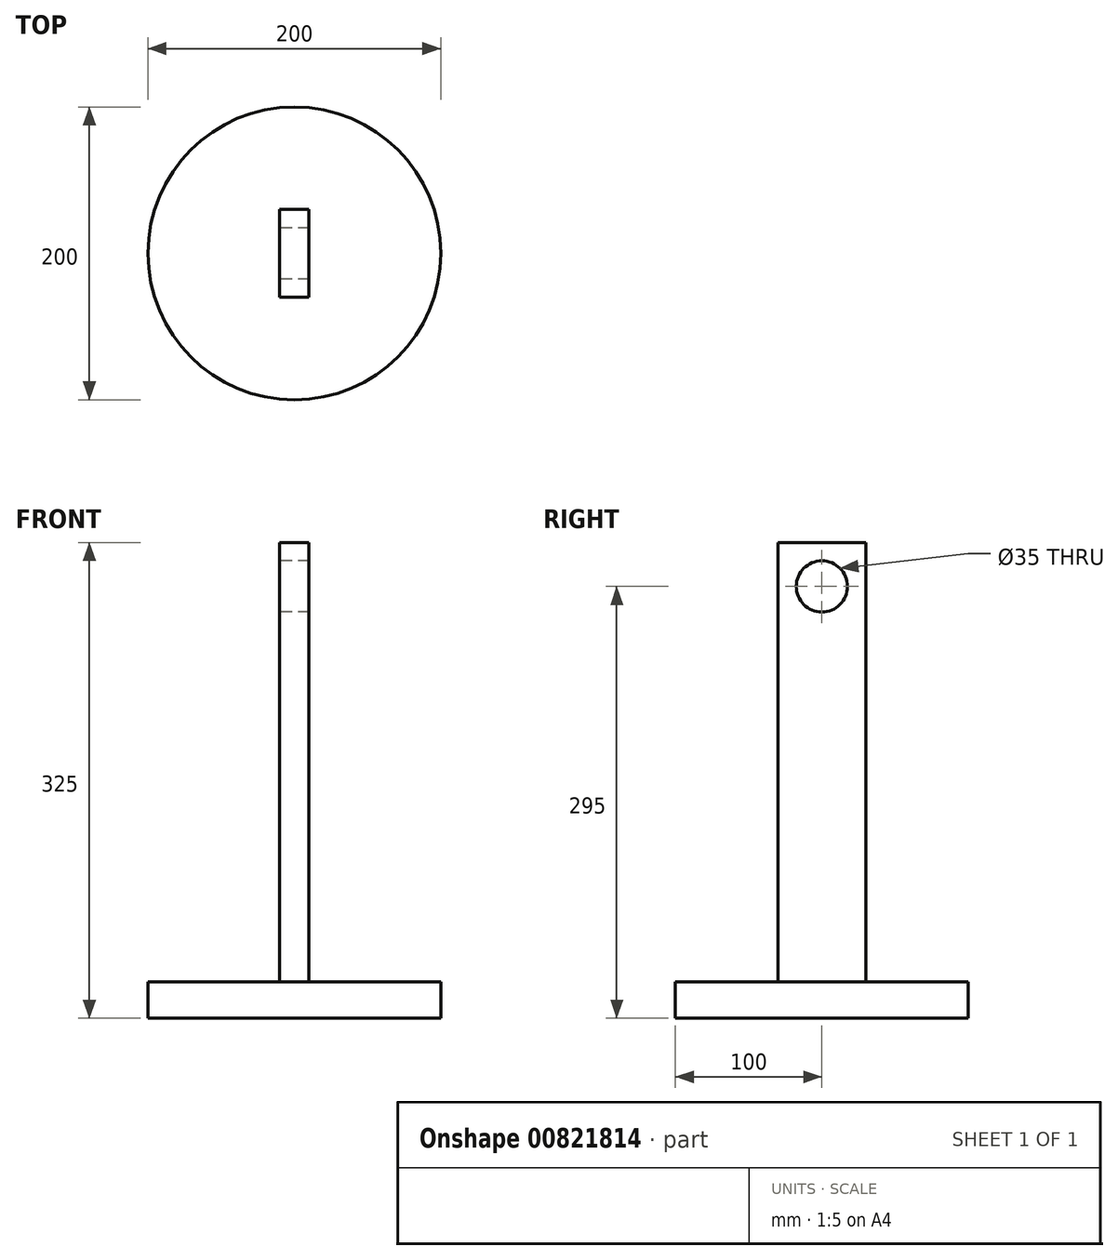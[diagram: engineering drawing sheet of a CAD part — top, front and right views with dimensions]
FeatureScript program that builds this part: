
annotation { "Feature Type Name" : "Feature", "Feature Type Description" : "" }
export const myFeature = defineFeature(function(context is Context, id is Id, definition is map)
    precondition{}
    {
        {
            var Q0;
            Q0=qCreatedBy(makeId("Top.planeOp"),FACE);
            var sketch = newSketch(context, id + "F0", { "sketchPlane" : qUnion([Q0])});
            skCircle(sketch, "E0", {"center": v(0, 0) * mm, "radius": 100 * mm});
            skSolve(sketch);
        }
        {
            var Q0;
            Q0=makeQuery(id+"F0.imprint","IMPRINT",FACE,{"disambiguationData":[TD([[makeQuery(id+"F0.imprint","IMPRINT",EDGE,{"derivedFrom":sQuery(id+"F0.wireOp",EDGE,"E0")}),1.0]])]});
            extrude(context, id + "F1", {"entities" : qUnion([Q0]), "depth" : 25 * mm, "offsetDistance" : 25 * mm});
        }
        {
            var Q0;
            Q0=makeQuery(id+"F1.opExtrude","CAP_FACE",FACE,{"disambiguationData":[OSD([sQuery(id+"F0.wireOp",EDGE,"E0")])],"isStart":false});
            var sketch = newSketch(context, id + "F2", { "sketchPlane" : qUnion([Q0])});
            skLineSegment(sketch, "E1.bottom", {"start": v(10, -30) * mm, "end": v(-10, -30) * mm});
            skLineSegment(sketch, "E1.top", {"start": v(10, 30) * mm, "end": v(-10, 30) * mm});
            skLineSegment(sketch, "E1.left", {"start": v(10, -30) * mm, "end": v(10, 30) * mm});
            skLineSegment(sketch, "E1.right", {"start": v(-10, -30) * mm, "end": v(-10, 30) * mm});
            skPoint(sketch, "E1.middle", {"position": v(0, 0) * mm});
            skSolve(sketch);
        }
        {
            var Q0;
            Q0=makeQuery(id+"F2.imprint","IMPRINT",FACE,{"disambiguationData":[TD([[makeQuery(id+"F2.imprint","IMPRINT",EDGE,{"derivedFrom":sQuery(id+"F2.wireOp",EDGE,"E1.bottom")}),-1.0]])]});
            extrude(context, id + "F3", {"entities" : qUnion([Q0]), "operationType" : NewBodyOperationType.ADD, "depth" : 300 * mm, "offsetDistance" : 25 * mm});
        }
        {
            var Q0;
            Q0=makeQuery(id+"F3.opExtrude","SWEPT_FACE",FACE,{"disambiguationData":[OSD([sQuery(id+"F2.wireOp",EDGE,"E1.right")])]});
            var sketch = newSketch(context, id + "F4", { "sketchPlane" : qUnion([Q0])});
            skCircle(sketch, "E2", {"center": v(0, 295) * mm, "radius": 17.5 * mm});
            skPoint(sketch, "E2.centerSnap0", {"position": v(0, 325) * mm});
            skLineSegment(sketch, "E3", {"start": v(-30, 325) * mm, "end": v(30, 265) * mm, "construction": true});
            skSolve(sketch);
        }
        {
            var Q0;
            Q0=makeQuery(id+"F4.imprint","IMPRINT",FACE,{"disambiguationData":[TD([[makeQuery(id+"F4.imprint","IMPRINT",EDGE,{"derivedFrom":sQuery(id+"F4.wireOp",EDGE,"E2")}),1.0]])]});
            extrude(context, id + "F5", {"entities" : qUnion([Q0]), "operationType" : NewBodyOperationType.REMOVE, "endBound" : BoundingType.UP_TO_NEXT, "oppositeDirection" : true, "depth" : 25 * mm, "offsetDistance" : 25 * mm});
        }
    });
